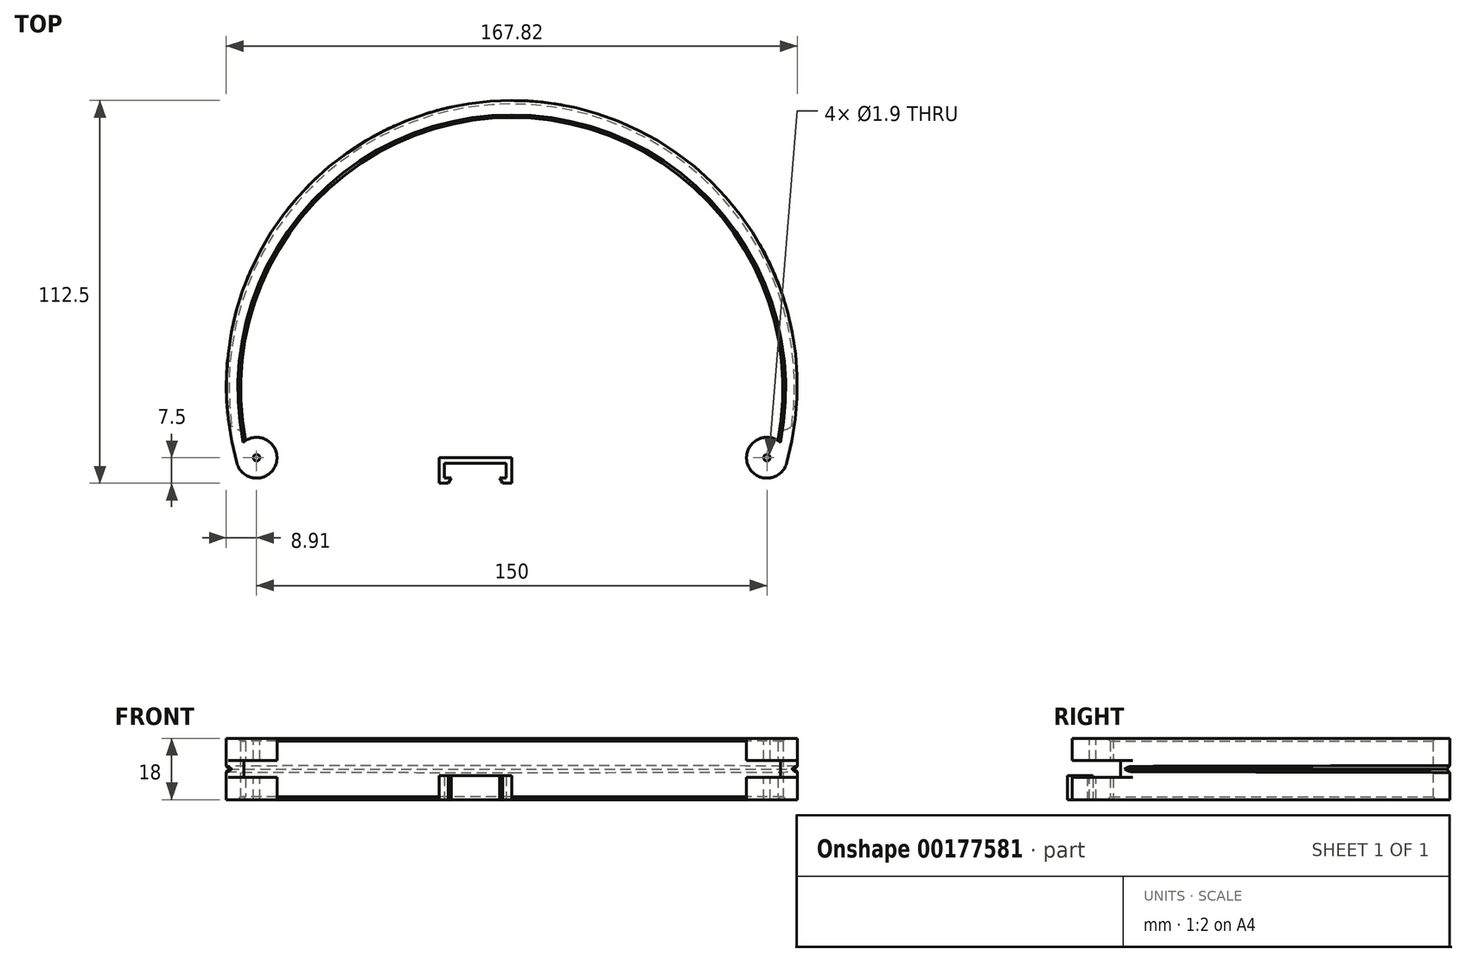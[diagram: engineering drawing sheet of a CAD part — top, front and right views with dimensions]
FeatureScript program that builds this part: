
annotation { "Feature Type Name" : "Feature", "Feature Type Description" : "" }
export const myFeature = defineFeature(function(context is Context, id is Id, definition is map)
    precondition{}
    {
        {
            var Q0;
            Q0=qCreatedBy(makeId("Top.planeOp"),FACE);
            var sketch = newSketch(context, id + "F0", { "sketchPlane" : qUnion([Q0])});
            skCircle(sketch, "E0", {"center": v(-75, 0) * mm, "radius": 6 * mm});
            skPoint(sketch, "E1", {"position": v(0, 105) * mm});
            skCircle(sketch, "E2", {"center": v(75, 0) * mm, "radius": 6 * mm});
            skArc(sketch, "E3", {"start": v(80.78, -1.62) * mm, "mid": v(0, 105) * mm, "end": v(-80.78, -1.62) * mm});
            skLineSegment(sketch, "E4", {"start": v(-75, 0) * mm, "end": v(-80.78, -1.62) * mm});
            skLineSegment(sketch, "E5", {"start": v(75, 0) * mm, "end": v(80.78, -1.62) * mm});
            skPoint(sketch, "E6", {"position": v(-76.93, -0.54) * mm});
            skPoint(sketch, "E7", {"position": v(76.93, -0.54) * mm});
            skLineSegment(sketch, "E8", {"start": v(0, 105) * mm, "end": v(0, 100) * mm});
            skArc(sketch, "E9", {"start": v(76.93, -0.54) * mm, "mid": v(0, 100) * mm, "end": v(-76.93, -0.54) * mm});
            skSolve(sketch);
        }
        {
            assignVariable(context, id + "F1", {"name" : "THICKNESS", "anyValue" : 18});
        }
        {
            var Q0;
            Q0 = qSketchRegion(id + "F0", true);
            extrude(context, id + "F2", {"entities" : qUnion([Q0]), "depth" : (getVariable(context, 'THICKNESS')) * mm});
        }
        {
            var Q0;
            Q0=makeQuery(id+"F2.opExtrude","CAP_FACE",FACE,{"disambiguationData":[OSD([sQuery(id+"F0.wireOp",EDGE,"E0"),sQuery(id+"F0.wireOp",EDGE,"E2"),sQuery(id+"F0.wireOp",EDGE,"E3"),sQuery(id+"F0.wireOp",EDGE,"E9")])],"isStart":false});
            cPlane(context, id + "F3", {"entities" : qUnion([Q0]), "cplaneType" : CPlaneType.OFFSET, "offset" : (getVariable(context, 'THICKNESS') / 2) * mm, "oppositeDirection" : true, "width" : 150 * mm, "height" : 150 * mm});
        }
        {
            var Q0;
            Q0=qCreatedBy(id+"F3.planeOp",FACE);
            var sketch = newSketch(context, id + "F4", { "sketchPlane" : qUnion([Q0])});
            skPoint(sketch, "E10", {"position": v(-75, 0) * mm});
            skPoint(sketch, "E11", {"position": v(75, 0) * mm});
            skCircle(sketch, "E12", {"center": v(-75, 0) * mm, "radius": 9 * mm});
            skCircle(sketch, "E13", {"center": v(75, 0) * mm, "radius": 9 * mm});
            skSolve(sketch);
        }
        {
            var Q0;
            Q0 = qSketchRegion(id + "F4", true);
            extrude(context, id + "F5", {"entities" : qUnion([Q0]), "operationType" : NewBodyOperationType.REMOVE, "endBound" : BoundingType.SYMMETRIC, "depth" : 5 * mm});
        }
        {
            var Q0;
            Q0=qCreatedBy(id+"F3.planeOp",FACE);
            var sketch = newSketch(context, id + "F6", { "sketchPlane" : qUnion([Q0])});
            skPoint(sketch, "E14", {"position": v(-75, 0) * mm});
            skPoint(sketch, "E15", {"position": v(75, 0) * mm});
            skCircle(sketch, "E16", {"center": v(-75, 0) * mm, "radius": 4.75 * mm, "construction": true});
            skCircle(sketch, "E17", {"center": v(75, 0) * mm, "radius": 4.75 * mm, "construction": true});
            skPoint(sketch, "E18", {"position": v(0, 103.5) * mm});
            skArc(sketch, "E19", {"start": v(79.58, -1.27) * mm, "mid": v(0, 103.5) * mm, "end": v(-79.58, -1.27) * mm});
            skArc(sketch, "E20", {"start": v(79.58, -1.27) * mm, "mid": v(0, 135) * mm, "end": v(-79.58, -1.27) * mm});
            skSolve(sketch);
        }
        {
            var Q0;
            Q0 = qSketchRegion(id + "F6", true);
            extrude(context, id + "F7", {"entities" : qUnion([Q0]), "operationType" : NewBodyOperationType.REMOVE, "endBound" : BoundingType.SYMMETRIC, "oppositeDirection" : true, "depth" : 2 * mm});
        }
        {
            var Q0;
            Q0=makeQuery(id+"F5.boolean.opBoolean","INTERSECT",EDGE,{"derivedFrom":[makeQuery(id+"F2.opExtrude","SWEPT_FACE",FACE,{"disambiguationData":[OSD([sQuery(id+"F0.wireOp",EDGE,"E3")])]}),makeQuery(id+"F5.opExtrude","SWEPT_FACE",FACE,{"disambiguationData":[OSD([sQuery(id+"F4.wireOp",EDGE,"E13")])]})]});
            var Q1;
            Q1=makeQuery(id+"F5.boolean.opBoolean","INTERSECT",EDGE,{"derivedFrom":[makeQuery(id+"F2.opExtrude","SWEPT_FACE",FACE,{"disambiguationData":[OSD([sQuery(id+"F0.wireOp",EDGE,"E3")])]}),makeQuery(id+"F5.opExtrude","SWEPT_FACE",FACE,{"disambiguationData":[OSD([sQuery(id+"F4.wireOp",EDGE,"E12")])]})]});
            fillet(context, id + "F8", {"entities" : qUnion([Q0, Q1]), "radius" : 4 * mm, "tangentPropagation" : true, "allowEdgeOverflow" : false});
        }
        {
            var Q0;
            Q0=makeQuery(id+"F7.boolean.opBoolean","COPY",EDGE,{"derivedFrom":makeQuery(id+"F7.opExtrude","CAP_EDGE",EDGE,{"disambiguationData":[OSD([sQuery(id+"F6.wireOp",EDGE,"E19")])],"isStart":true})});
            var Q1;
            Q1=makeQuery(id+"F7.boolean.opBoolean","COPY",EDGE,{"derivedFrom":makeQuery(id+"F7.opExtrude","CAP_EDGE",EDGE,{"disambiguationData":[OSD([sQuery(id+"F6.wireOp",EDGE,"E19")])],"isStart":false})});
            chamfer(context, id + "F9", {"entities" : qUnion([Q0, Q1]), "width" : 1.5 * mm, "tangentPropagation" : true});
        }
        {
            var Q0;
            Q0=makeQuery(id+"F2.opExtrude","CAP_FACE",FACE,{"disambiguationData":[OSD([sQuery(id+"F0.wireOp",EDGE,"E0"),sQuery(id+"F0.wireOp",EDGE,"E2"),sQuery(id+"F0.wireOp",EDGE,"E3"),sQuery(id+"F0.wireOp",EDGE,"E9")])],"isStart":false});
            var sketch = newSketch(context, id + "F10", { "sketchPlane" : qUnion([Q0])});
            skCircle(sketch, "E21", {"center": v(-75, 0) * mm, "radius": 0.95 * mm});
            skCircle(sketch, "E22", {"center": v(75, 0) * mm, "radius": 0.95 * mm});
            skSolve(sketch);
        }
        {
            var Q0;
            Q0 = qSketchRegion(id + "F10", true);
            var Q1;
            Q1=makeQuery(id+"F2.opExtrude","CAP_FACE",FACE,{"disambiguationData":[OSD([sQuery(id+"F0.wireOp",EDGE,"E0"),sQuery(id+"F0.wireOp",EDGE,"E2"),sQuery(id+"F0.wireOp",EDGE,"E3"),sQuery(id+"F0.wireOp",EDGE,"E9")])],"isStart":true});
            extrude(context, id + "F11", {"entities" : qUnion([Q0]), "operationType" : NewBodyOperationType.REMOVE, "endBound" : BoundingType.UP_TO_SURFACE, "oppositeDirection" : true, "endBoundEntityFace" : qUnion([Q1]), "depth" : 25 * mm});
        }
        {
            var Q0;
            Q0=makeQuery(id+"F2.opExtrude","CAP_EDGE",EDGE,{"disambiguationData":[OSD([sQuery(id+"F0.wireOp",EDGE,"E9")])],"isStart":false});
            var Q1;
            Q1=makeQuery(id+"F2.opExtrude","CAP_EDGE",EDGE,{"disambiguationData":[OSD([sQuery(id+"F0.wireOp",EDGE,"E9")])],"isStart":true});
            chamfer(context, id + "F12", {"entities" : qUnion([Q0, Q1]), "width" : 0.8 * mm, "tangentPropagation" : true});
        }
        {
            var Q0;
            {var subQ0=makeQuery(id+"F2.opExtrude","SWEPT_FACE",FACE,{"disambiguationData":[OSD([sQuery(id+"F0.wireOp",EDGE,"E3")])]});var subQ1=sQuery(id+"F4.wireOp",EDGE,"E13");var subQ2=makeQuery(id+"F5.opExtrude","SWEPT_FACE",FACE,{"disambiguationData":[OSD([subQ1])]});Q0=makeQuery(id+"F8.opFillet","BLEND_EDGE",EDGE,{"blendedFrom":[makeQuery(id+"F7.boolean.opBoolean","SPLIT",EDGE,{"disambiguationData":[TD([makeQuery(id+"F5.boolean.opBoolean","COPY",FACE,{"derivedFrom":makeQuery(id+"F5.opExtrude","CAP_FACE",FACE,{"disambiguationData":[OSD([subQ1])],"isStart":true})})])],"derivedFrom":makeQuery(id+"F5.boolean.opBoolean","INTERSECT",EDGE,{"derivedFrom":[subQ0,subQ2]})}),makeQuery(id+"F2.opExtrude","SWEPT_FACE",FACE,{"disambiguationData":[OSD([sQuery(id+"F0.wireOp",EDGE,"E9")])]})],"blendedInto":[makeQuery(id+"F2.opExtrude","SWEPT_FACE",FACE,{"disambiguationData":[OSD([sQuery(id+"F0.wireOp",EDGE,"E9")])]})]});}
            var Q1;
            {var subQ0=makeQuery(id+"F2.opExtrude","SWEPT_FACE",FACE,{"disambiguationData":[OSD([sQuery(id+"F0.wireOp",EDGE,"E3")])]});var subQ1=sQuery(id+"F4.wireOp",EDGE,"E12");var subQ2=makeQuery(id+"F5.opExtrude","SWEPT_FACE",FACE,{"disambiguationData":[OSD([subQ1])]});Q1=makeQuery(id+"F8.opFillet","BLEND_EDGE",EDGE,{"blendedFrom":[makeQuery(id+"F7.boolean.opBoolean","SPLIT",EDGE,{"disambiguationData":[TD([makeQuery(id+"F5.boolean.opBoolean","COPY",FACE,{"derivedFrom":makeQuery(id+"F5.opExtrude","CAP_FACE",FACE,{"disambiguationData":[OSD([subQ1])],"isStart":false})})])],"derivedFrom":makeQuery(id+"F5.boolean.opBoolean","INTERSECT",EDGE,{"derivedFrom":[subQ0,subQ2]})}),makeQuery(id+"F2.opExtrude","SWEPT_FACE",FACE,{"disambiguationData":[OSD([sQuery(id+"F0.wireOp",EDGE,"E9")])]})],"blendedInto":[makeQuery(id+"F2.opExtrude","SWEPT_FACE",FACE,{"disambiguationData":[OSD([sQuery(id+"F0.wireOp",EDGE,"E9")])]})]});}
            fillet(context, id + "F13", {"entities" : qUnion([Q0, Q1]), "radius" : 1 * mm, "tangentPropagation" : true, "allowEdgeOverflow" : false});
        }
        {
            var Q0;
            Q0=qCreatedBy(makeId("Top.planeOp"),FACE);
            var sketch = newSketch(context, id + "F14", { "sketchPlane" : qUnion([Q0])});
            skLineSegment(sketch, "E23", {"start": v(-17.8, -5.9) * mm, "end": v(-18.72, -7.5) * mm});
            skLineSegment(sketch, "E24", {"start": v(-18.72, -7.5) * mm, "end": v(-21.4, -7.5) * mm});
            skLineSegment(sketch, "E25", {"start": v(-21.4, -7.5) * mm, "end": v(-21.4, 0) * mm});
            skLineSegment(sketch, "E26", {"start": v(-21.4, 0) * mm, "end": v(0, 0) * mm});
            skLineSegment(sketch, "E27", {"start": v(0, 0) * mm, "end": v(0, -7.5) * mm});
            skLineSegment(sketch, "E28", {"start": v(0, -7.5) * mm, "end": v(-2.68, -7.5) * mm});
            skLineSegment(sketch, "E29", {"start": v(-2.68, -7.5) * mm, "end": v(-3.6, -5.9) * mm});
            skLineSegment(sketch, "E30", {"start": v(-3.6, -5.9) * mm, "end": v(-1.6, -5.9) * mm});
            skLineSegment(sketch, "E31", {"start": v(-1.6, -5.9) * mm, "end": v(-1.6, -1.6) * mm});
            skLineSegment(sketch, "E32", {"start": v(-1.6, -1.6) * mm, "end": v(-19.8, -1.6) * mm});
            skLineSegment(sketch, "E33", {"start": v(-19.8, -1.6) * mm, "end": v(-19.8, -5.9) * mm});
            skLineSegment(sketch, "E34", {"start": v(-19.8, -5.9) * mm, "end": v(-17.8, -5.9) * mm});
            skPoint(sketch, "E35", {"position": v(-10.7, 0) * mm});
            skPoint(sketch, "E36", {"position": v(-10.7, -1.6) * mm});
            skSolve(sketch);
        }
        {
            var Q0;
            Q0 = qSketchRegion(id + "F14", true);
            extrude(context, id + "F15", {"entities" : qUnion([Q0]), "depth" : 7 * mm});
        }
    });
